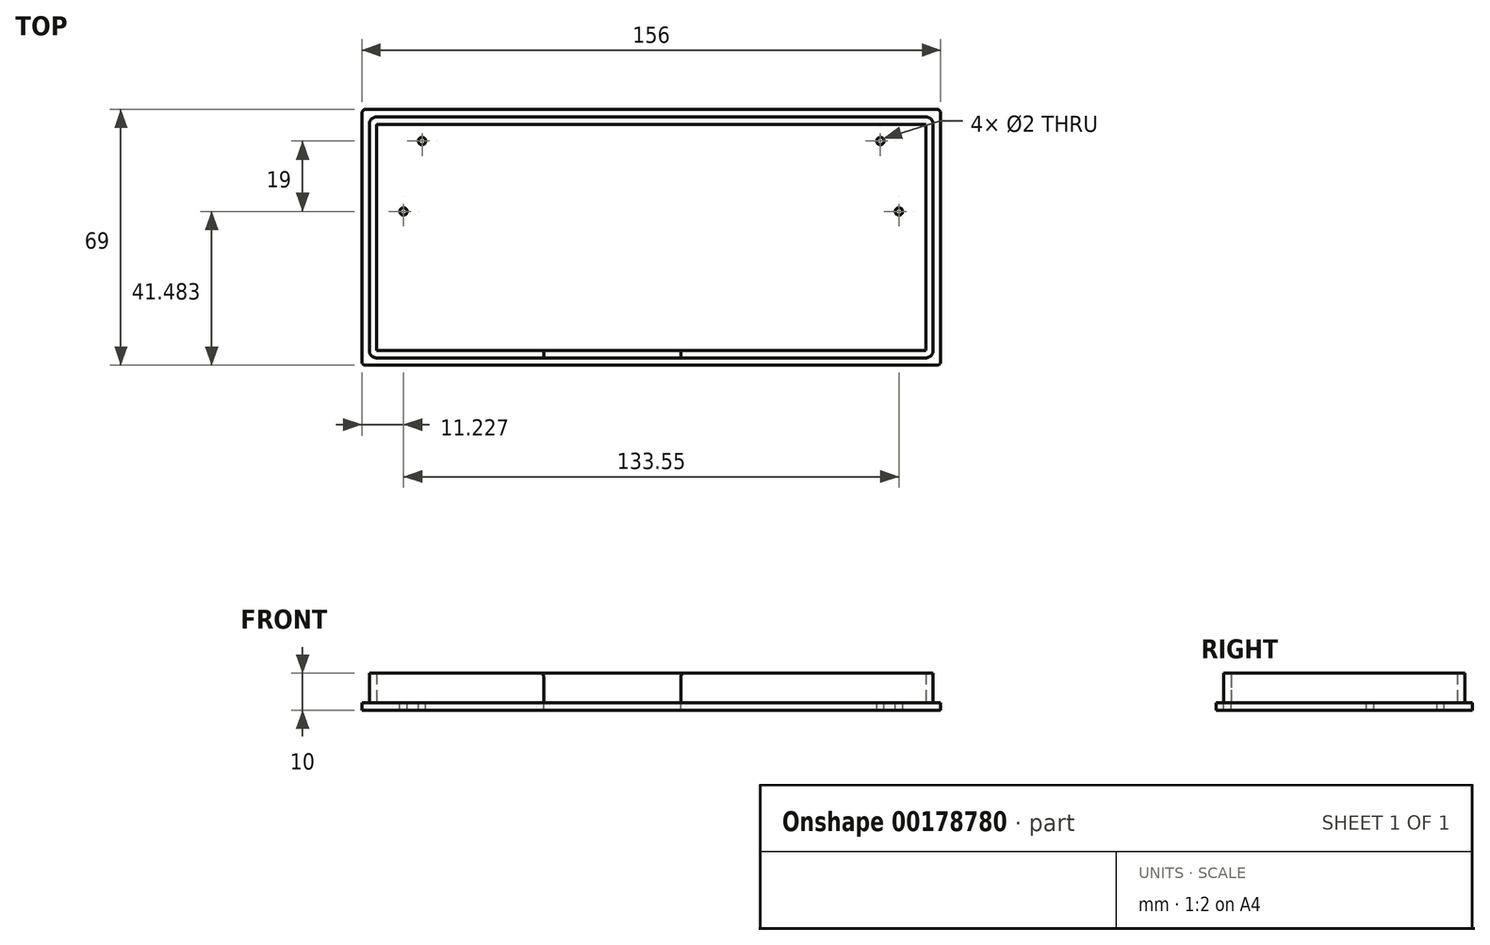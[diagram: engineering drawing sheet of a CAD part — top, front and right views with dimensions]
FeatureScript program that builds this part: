
annotation { "Feature Type Name" : "Feature", "Feature Type Description" : "" }
export const myFeature = defineFeature(function(context is Context, id is Id, definition is map)
    precondition{}
    {
        {
            var Q0;
            Q0=qCreatedBy(makeId("Top.planeOp"),FACE);
            var sketch = newSketch(context, id + "F0", { "sketchPlane" : qUnion([Q0])});
            skLineSegment(sketch, "E0.0", {"start": v(102.2, 36.23) * mm, "end": v(-49.8, 36.23) * mm});
            skLineSegment(sketch, "E0.1", {"start": v(102.2, -28.77) * mm, "end": v(102.2, 36.23) * mm});
            skLineSegment(sketch, "E0.2", {"start": v(-49.8, -28.77) * mm, "end": v(102.2, -28.77) * mm});
            skLineSegment(sketch, "E0.3", {"start": v(-49.8, 36.23) * mm, "end": v(-49.8, -28.77) * mm});
            skLineSegment(sketch, "E1.0", {"start": v(104.2, 38.23) * mm, "end": v(-51.8, 38.23) * mm});
            skLineSegment(sketch, "E1.1", {"start": v(104.2, -30.77) * mm, "end": v(104.2, 38.23) * mm});
            skLineSegment(sketch, "E1.2", {"start": v(-51.8, -30.77) * mm, "end": v(104.2, -30.77) * mm});
            skLineSegment(sketch, "E1.3", {"start": v(-51.8, 38.23) * mm, "end": v(-51.8, -30.77) * mm});
            skLineSegment(sketch, "E2.0", {"start": v(-47.8, 34.23) * mm, "end": v(-47.8, -26.77) * mm});
            skLineSegment(sketch, "E2.1", {"start": v(100.2, 34.23) * mm, "end": v(-47.8, 34.23) * mm});
            skLineSegment(sketch, "E2.2", {"start": v(100.2, -26.77) * mm, "end": v(100.2, 34.23) * mm});
            skLineSegment(sketch, "E2.3", {"start": v(-47.8, -26.77) * mm, "end": v(100.2, -26.77) * mm});
            skLineSegment(sketch, "E3.0", {"start": v(-2.8, 38.23) * mm, "end": v(-2.8, -30.77) * mm, "construction": true});
            skLineSegment(sketch, "E4.0", {"start": v(34.2, 38.23) * mm, "end": v(34.2, -30.77) * mm, "construction": true});
            skLineSegment(sketch, "E5.bottom", {"start": v(-2.8, -26.77) * mm, "end": v(34.2, -26.77) * mm});
            skLineSegment(sketch, "E5.top", {"start": v(-2.8, -28.77) * mm, "end": v(34.2, -28.77) * mm});
            skLineSegment(sketch, "E5.left", {"start": v(-2.8, -26.77) * mm, "end": v(-2.8, -28.77) * mm});
            skLineSegment(sketch, "E5.right", {"start": v(34.2, -26.77) * mm, "end": v(34.2, -28.77) * mm});
            skLineSegment(sketch, "E6.0", {"start": v(90.48, 10.71) * mm, "end": v(95.48, 10.71) * mm, "construction": true});
            skCircle(sketch, "E7", {"center": v(92.98, 10.71) * mm, "radius": 1 * mm});
            skPoint(sketch, "E8.end.orphan", {"position": v(127.93, 18.41) * mm});
            skPoint(sketch, "E9.start.orphan", {"position": v(127.93, 23.41) * mm});
            skLineSegment(sketch, "E10.0", {"start": v(90.48, 29.71) * mm, "end": v(85.48, 29.71) * mm, "construction": true});
            skLineSegment(sketch, "E11.0", {"start": v(87.98, 32.21) * mm, "end": v(87.98, 28.71) * mm, "construction": true});
            skCircle(sketch, "E12", {"center": v(87.98, 29.71) * mm, "radius": 1 * mm});
            skLineSegment(sketch, "E13.0", {"start": v(104.2, 32.23) * mm, "end": v(100.2, 32.23) * mm, "construction": true});
            skLineSegment(sketch, "E14.0", {"start": v(26.2, -30.77) * mm, "end": v(26.2, 38.23) * mm, "construction": true});
            skLineSegment(sketch, "E15.MirrorCS", {"start": v(-38.07, 10.71) * mm, "end": v(-43.07, 10.71) * mm, "construction": true});
            skLineSegment(sketch, "E16.MirrorCS", {"start": v(-35.57, 32.21) * mm, "end": v(-35.57, 27.21) * mm, "construction": true});
            skLineSegment(sketch, "E17.MirrorCS", {"start": v(-38.07, 29.71) * mm, "end": v(-33.07, 29.71) * mm, "construction": true});
            skCircle(sketch, "E18.MirrorC", {"center": v(-35.57, 29.71) * mm, "radius": 1 * mm});
            skCircle(sketch, "E19.MirrorC", {"center": v(-40.57, 10.71) * mm, "radius": 1 * mm});
            skLineSegment(sketch, "E20.MirrorCS", {"start": v(-51.8, -30.77) * mm, "end": v(-51.8, 38.23) * mm, "construction": true});
            skLineSegment(sketch, "E21.trimOffspring", {"start": v(34.2, 32.23) * mm, "end": v(-2.8, 32.23) * mm, "construction": true});
            skPoint(sketch, "E22.orphan", {"position": v(87.98, 27.21) * mm});
            skLineSegment(sketch, "E23.trimOffspring", {"start": v(-47.8, 32.23) * mm, "end": v(-51.8, 32.23) * mm, "construction": true});
            skSolve(sketch);
        }
        {
            var Q0;
            Q0=makeQuery(id+"F0.imprint","IMPRINT",FACE,{"disambiguationData":[TD([[makeQuery(id+"F0.imprint","IMPRINT",EDGE,{"derivedFrom":sQuery(id+"F0.wireOp",EDGE,"E0.0")}),-1.0]])]});
            var Q1;
            Q1=makeQuery(id+"F0.imprint","IMPRINT",FACE,{"disambiguationData":[TD([[makeQuery(id+"F0.imprint","IMPRINT",EDGE,{"derivedFrom":sQuery(id+"F0.wireOp",EDGE,"E0.0")}),1.0]])]});
            var Q2;
            {var subQ1=sQuery(id+"F0.wireOp",EDGE,"E2.0");Q2=makeQuery(id+"F0.imprint","IMPRINT",FACE,{"disambiguationData":[TD([[makeQuery(id+"F0.imprint","IMPRINT",EDGE,{"derivedFrom":subQ1}),1.0]])]});}
            var Q3;
            Q3=makeQuery(id+"F0.imprint","IMPRINT",FACE,{"disambiguationData":[TD([[makeQuery(id+"F0.imprint","IMPRINT",EDGE,{"derivedFrom":sQuery(id+"F0.wireOp",EDGE,"E5.bottom")}),-1.0]])]});
            extrude(context, id + "F1", {"entities" : qUnion([Q0, Q1, Q2, Q3]), "oppositeDirection" : true, "depth" : 2 * mm});
        }
        {
            var Q0;
            Q0=makeQuery(id+"F0.imprint","IMPRINT",FACE,{"disambiguationData":[TD([[makeQuery(id+"F0.imprint","IMPRINT",EDGE,{"derivedFrom":sQuery(id+"F0.wireOp",EDGE,"E0.0")}),1.0]])]});
            extrude(context, id + "F2", {"entities" : qUnion([Q0]), "operationType" : NewBodyOperationType.ADD, "depth" : 8 * mm});
        }
        {
            var Q0;
            Q0=makeQuery(id+"F1.opExtrude","SWEPT_EDGE",EDGE,{"disambiguationData":[OSD([sQuery(id+"F0.wireOp",EDGE,"E1.0"),sQuery(id+"F0.wireOp",EDGE,"E1.3")])]});
            var Q1;
            Q1=makeQuery(id+"F1.opExtrude","SWEPT_EDGE",EDGE,{"disambiguationData":[OSD([sQuery(id+"F0.wireOp",EDGE,"E1.2"),sQuery(id+"F0.wireOp",EDGE,"E1.3")])]});
            var Q2;
            Q2=makeQuery(id+"F1.opExtrude","SWEPT_EDGE",EDGE,{"disambiguationData":[OSD([sQuery(id+"F0.wireOp",EDGE,"E1.1"),sQuery(id+"F0.wireOp",EDGE,"E1.2")])]});
            var Q3;
            Q3=makeQuery(id+"F1.opExtrude","SWEPT_EDGE",EDGE,{"disambiguationData":[OSD([sQuery(id+"F0.wireOp",EDGE,"E1.0"),sQuery(id+"F0.wireOp",EDGE,"E1.1")])]});
            var Q4;
            Q4=makeQuery(id+"F2.opExtrude","CAP_EDGE",EDGE,{"disambiguationData":[OSD([sQuery(id+"F0.wireOp",EDGE,"E5.right")])],"isStart":false});
            var Q5;
            Q5=makeQuery(id+"F2.opExtrude","CAP_EDGE",EDGE,{"disambiguationData":[OSD([sQuery(id+"F0.wireOp",EDGE,"E5.left")])],"isStart":false});
            var Q6;
            Q6=makeQuery(id+"F2.opExtrude","CAP_EDGE",EDGE,{"disambiguationData":[OSD([sQuery(id+"F0.wireOp",EDGE,"E5.right")])],"isStart":true});
            var Q7;
            Q7=makeQuery(id+"F2.opExtrude","CAP_EDGE",EDGE,{"disambiguationData":[OSD([sQuery(id+"F0.wireOp",EDGE,"E5.left")])],"isStart":true});
            fillet(context, id + "F3", {"entities" : qUnion([Q0, Q1, Q2, Q3, Q4, Q5, Q6, Q7]), "radius" : 1 * mm, "tangentPropagation" : true, "allowEdgeOverflow" : false});
        }
        {
            var Q0;
            Q0=makeQuery(id+"F2.opExtrude","SWEPT_EDGE",EDGE,{"disambiguationData":[OSD([sQuery(id+"F0.wireOp",EDGE,"E0.2"),sQuery(id+"F0.wireOp",EDGE,"E0.3")])]});
            var Q1;
            Q1=makeQuery(id+"F2.opExtrude","SWEPT_EDGE",EDGE,{"disambiguationData":[OSD([sQuery(id+"F0.wireOp",EDGE,"E0.1"),sQuery(id+"F0.wireOp",EDGE,"E0.2")])]});
            var Q2;
            Q2=makeQuery(id+"F2.opExtrude","SWEPT_EDGE",EDGE,{"disambiguationData":[OSD([sQuery(id+"F0.wireOp",EDGE,"E0.0"),sQuery(id+"F0.wireOp",EDGE,"E0.1")])]});
            var Q3;
            Q3=makeQuery(id+"F2.opExtrude","SWEPT_EDGE",EDGE,{"disambiguationData":[OSD([sQuery(id+"F0.wireOp",EDGE,"E0.0"),sQuery(id+"F0.wireOp",EDGE,"E0.3")])]});
            fillet(context, id + "F4", {"entities" : qUnion([Q0, Q1, Q2, Q3]), "radius" : 2 * mm, "tangentPropagation" : true, "allowEdgeOverflow" : false});
        }
    });
